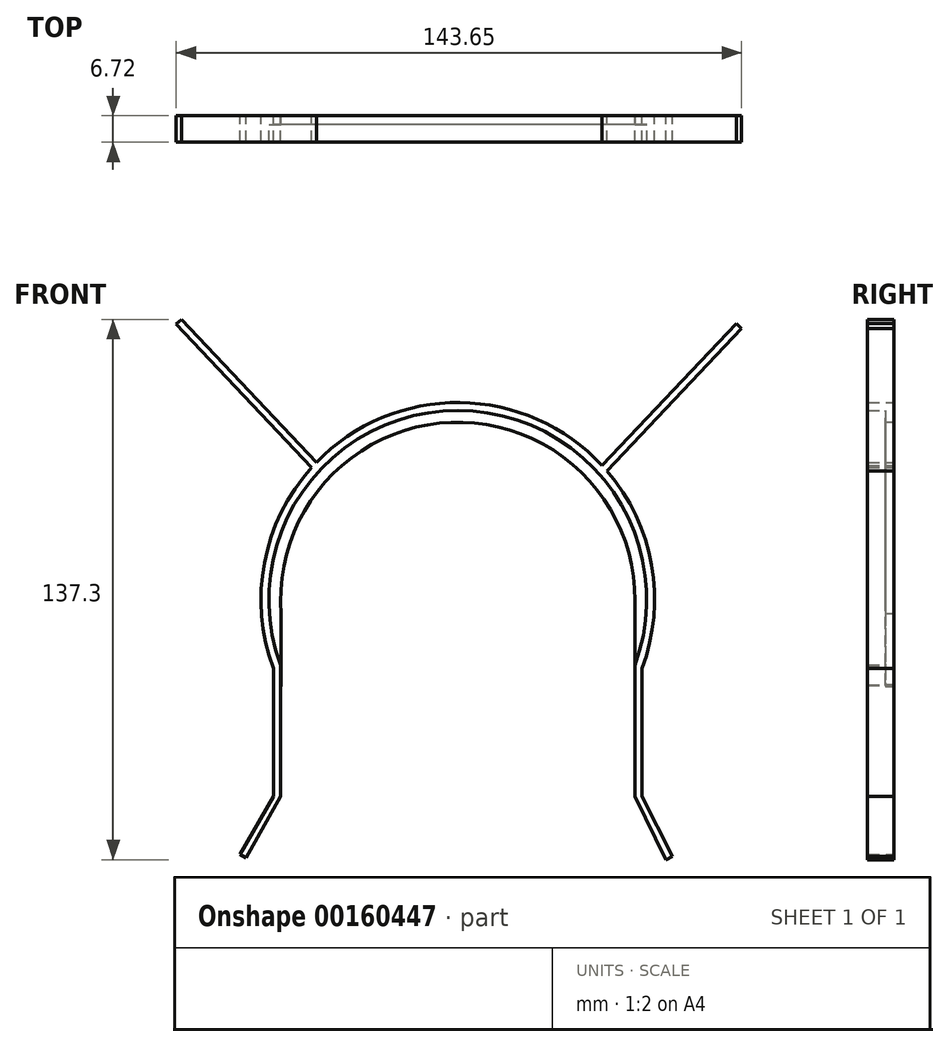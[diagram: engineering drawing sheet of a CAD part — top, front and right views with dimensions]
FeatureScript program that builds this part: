
annotation { "Feature Type Name" : "Feature", "Feature Type Description" : "" }
export const myFeature = defineFeature(function(context is Context, id is Id, definition is map)
    precondition{}
    {
        {
            var Q0;
            Q0=qCreatedBy(makeId("Front.planeOp"),FACE);
            var sketch = newSketch(context, id + "F0", { "sketchPlane" : qUnion([Q0])});
            skLineSegment(sketch, "E0", {"start": v(-45, 0) * mm, "end": v(-45, -50) * mm});
            skLineSegment(sketch, "E1", {"start": v(-45, -50) * mm, "end": v(-46.8, -50) * mm});
            skLineSegment(sketch, "E2", {"start": v(-46.8, -50) * mm, "end": v(-46.8, 0) * mm});
            skLineSegment(sketch, "E3", {"start": v(-46.8, 0) * mm, "end": v(-45, 0) * mm});
            skLineSegment(sketch, "E4", {"start": v(45, 0) * mm, "end": v(45, -50) * mm});
            skLineSegment(sketch, "E5", {"start": v(45, -50) * mm, "end": v(46.8, -50) * mm});
            skLineSegment(sketch, "E6", {"start": v(46.8, -50) * mm, "end": v(46.8, 0) * mm});
            skLineSegment(sketch, "E7", {"start": v(46.8, 0) * mm, "end": v(45, 0) * mm});
            skCircle(sketch, "E8", {"center": v(0, 0) * mm, "radius": 50 * mm});
            skLineSegment(sketch, "E9", {"start": v(-37.12, 33.5) * mm, "end": v(-71.54, 69.91) * mm});
            skLineSegment(sketch, "E10", {"start": v(-71.54, 69.91) * mm, "end": v(-70.23, 71.15) * mm});
            skLineSegment(sketch, "E11", {"start": v(-70.23, 71.15) * mm, "end": v(-35.89, 34.82) * mm});
            skLineSegment(sketch, "E12", {"start": v(36.69, 33.97) * mm, "end": v(70.8, 70.07) * mm});
            skLineSegment(sketch, "E13", {"start": v(70.8, 70.07) * mm, "end": v(72.1, 68.83) * mm});
            skLineSegment(sketch, "E14", {"start": v(72.1, 68.83) * mm, "end": v(37.77, 32.5) * mm});
            skLineSegment(sketch, "E15", {"start": v(-46.8, -50) * mm, "end": v(-55.36, -64.8) * mm});
            skLineSegment(sketch, "E16", {"start": v(-55.36, -64.8) * mm, "end": v(-53.8, -65.7) * mm});
            skLineSegment(sketch, "E17", {"start": v(-53.8, -65.7) * mm, "end": v(-45, -50) * mm});
            skLineSegment(sketch, "E18", {"start": v(45, -50) * mm, "end": v(52.95, -66.15) * mm});
            skLineSegment(sketch, "E19", {"start": v(52.95, -66.15) * mm, "end": v(54.56, -65.36) * mm});
            skLineSegment(sketch, "E20", {"start": v(54.56, -65.36) * mm, "end": v(46.8, -50) * mm});
            skSolve(sketch);
        }
        {
            var Q0;
            Q0=qCreatedBy(makeId("Front.planeOp"),FACE);
            var sketch = newSketch(context, id + "F1", { "sketchPlane" : qUnion([Q0])});
            skSolve(sketch);
        }
        {
            var Q0;
            Q0=qSketchRegion(id+"F1",true);
            var Q1;
            {var subQ0=sQuery(id+"F0.wireOp",EDGE,"E1");Q1=makeQuery(id+"F0.imprint","IMPRINT",FACE,{"disambiguationData":[TD([[makeQuery(id+"F0.imprint","IMPRINT",EDGE,{"derivedFrom":subQ0}),-1.0]])]});}
            var Q2;
            {var subQ0=sQuery(id+"F0.wireOp",EDGE,"E3");Q2=makeQuery(id+"F0.imprint","IMPRINT",FACE,{"disambiguationData":[TD([[makeQuery(id+"F0.imprint","IMPRINT",EDGE,{"derivedFrom":subQ0}),-1.0]])]});}
            var Q3;
            {var subQ0=sQuery(id+"F0.wireOp",EDGE,"E7");Q3=makeQuery(id+"F0.imprint","IMPRINT",FACE,{"disambiguationData":[TD([[makeQuery(id+"F0.imprint","IMPRINT",EDGE,{"derivedFrom":subQ0}),1.0]])]});}
            var Q4;
            {var subQ0=sQuery(id+"F0.wireOp",EDGE,"E5");Q4=makeQuery(id+"F0.imprint","IMPRINT",FACE,{"disambiguationData":[TD([[makeQuery(id+"F0.imprint","IMPRINT",EDGE,{"derivedFrom":subQ0}),1.0]])]});}
            var Q5;
            {var subQ12=sQuery(id+"F0.wireOp",EDGE,"E3");Q5=makeQuery(id+"F0.imprint","IMPRINT",FACE,{"disambiguationData":[TD([[makeQuery(id+"F0.imprint","IMPRINT",EDGE,{"derivedFrom":subQ12}),1.0]])]});}
            var Q6;
            {var subQ0=sQuery(id+"F0.wireOp",EDGE,"E9");Q6=makeQuery(id+"F0.imprint","IMPRINT",FACE,{"disambiguationData":[TD([[makeQuery(id+"F0.imprint","IMPRINT",EDGE,{"derivedFrom":subQ0}),-1.0]])]});}
            var Q7;
            {var subQ0=sQuery(id+"F0.wireOp",EDGE,"E12");Q7=makeQuery(id+"F0.imprint","IMPRINT",FACE,{"disambiguationData":[TD([[makeQuery(id+"F0.imprint","IMPRINT",EDGE,{"derivedFrom":subQ0}),-1.0]])]});}
            var Q8;
            Q8=makeQuery(id+"F0.imprint","IMPRINT",FACE,{"disambiguationData":[TD([[makeQuery(id+"F0.imprint","IMPRINT",EDGE,{"derivedFrom":sQuery(id+"F0.wireOp",EDGE,"E1")}),1.0]])]});
            var Q9;
            Q9=makeQuery(id+"F0.imprint","IMPRINT",FACE,{"disambiguationData":[TD([[makeQuery(id+"F0.imprint","IMPRINT",EDGE,{"derivedFrom":sQuery(id+"F0.wireOp",EDGE,"E5")}),-1.0]])]});
            extrude(context, id + "F2", {"entities" : qUnion([Q0, Q1, Q2, Q3, Q4, Q5, Q6, Q7, Q8, Q9]), "depth" : .5 * mm});
        }
        {
            var Q0;
            Q0=qCreatedBy(makeId("Front.planeOp"),FACE);
            var sketch = newSketch(context, id + "F3", { "sketchPlane" : qUnion([Q0])});
            skCircle(sketch, "E21", {"center": v(0, 0) * mm, "radius": 48 * mm});
            skSolve(sketch);
        }
        {
            var Q0;
            Q0=qSketchRegion(id+"F3",true);
            extrude(context, id + "F4", {"entities" : qUnion([Q0]), "operationType" : NewBodyOperationType.REMOVE, "depth" : 2 * mm});
        }
        {
            var Q0;
            Q0=qCreatedBy(makeId("Front.planeOp"),FACE);
            var sketch = newSketch(context, id + "F5", { "sketchPlane" : qUnion([Q0])});
            skLineSegment(sketch, "E22", {"start": v(44.99, -22.07) * mm, "end": v(44.99, -3.86) * mm});
            skLineSegment(sketch, "E23", {"start": v(44.99, -3.86) * mm, "end": v(-45.01, -3.86) * mm});
            skLineSegment(sketch, "E24", {"start": v(-45.01, -3.86) * mm, "end": v(-45.01, -50.71) * mm});
            skLineSegment(sketch, "E25", {"start": v(-45.01, -50.71) * mm, "end": v(44.99, -50.71) * mm});
            skLineSegment(sketch, "E26", {"start": v(44.99, -50.71) * mm, "end": v(44.99, -22.07) * mm});
            skSolve(sketch);
        }
        {
            var Q0;
            Q0=qCreatedBy(makeId("Front.planeOp"),FACE);
            var sketch = newSketch(context, id + "F6", { "sketchPlane" : qUnion([Q0])});
            skSolve(sketch);
        }
        {
            var Q0;
            Q0=qSketchRegion(id+"F6",true);
            var Q1;
            Q1=makeQuery(id+"F5.imprint","IMPRINT",FACE,{"disambiguationData":[TD([[makeQuery(id+"F5.imprint","IMPRINT",EDGE,{"derivedFrom":sQuery(id+"F5.wireOp",EDGE,"E22")}),1.0]])]});
            extrude(context, id + "F7", {"entities" : qUnion([Q0, Q1]), "operationType" : NewBodyOperationType.REMOVE, "depth" : 2 * mm});
        }
        {
            var Q0;
            Q0=qCreatedBy(makeId("Front.planeOp"),FACE);
            var sketch = newSketch(context, id + "F8", { "sketchPlane" : qUnion([Q0])});
            skCircle(sketch, "E27", {"center": v(0, 0) * mm, "radius": 50 * mm});
            skSolve(sketch);
        }
        {
            var Q0;
            Q0=qSketchRegion(id+"F8",true);
            extrude(context, id + "F9", {"entities" : qUnion([Q0]), "operationType" : NewBodyOperationType.ADD, "oppositeDirection" : true, "depth" : 2.22 * mm});
        }
        {
            var Q0;
            Q0=qCreatedBy(makeId("Front.planeOp"),FACE);
            var sketch = newSketch(context, id + "F10", { "sketchPlane" : qUnion([Q0])});
            skCircle(sketch, "E28", {"center": v(0, 0) * mm, "radius": 45 * mm});
            skSolve(sketch);
        }
        {
            var Q0;
            Q0=qSketchRegion(id+"F10",true);
            extrude(context, id + "F11", {"entities" : qUnion([Q0]), "operationType" : NewBodyOperationType.REMOVE, "oppositeDirection" : true, "depth" : 2.22 * mm});
        }
        {
            var Q0;
            {var subQ0=sQuery(id+"F0.wireOp",EDGE,"E11");var subQ1=sQuery(id+"F0.wireOp",EDGE,"E8");var subQ2=sQuery(id+"F0.wireOp",EDGE,"E12");var subQ3=sQuery(id+"F0.wireOp",EDGE,"E6");var subQ4=sQuery(id+"F0.wireOp",EDGE,"E5");var subQ5=sQuery(id+"F0.wireOp",EDGE,"E4");var subQ6=sQuery(id+"F0.wireOp",EDGE,"E9");var subQ7=sQuery(id+"F0.wireOp",EDGE,"E2");var subQ8=sQuery(id+"F0.wireOp",EDGE,"E0");var subQ9=sQuery(id+"F0.wireOp",EDGE,"E14");Q0=makeQuery(id+"F9.boolean.opBoolean","SPLIT",FACE,{"disambiguationData":[TD([makeQuery(id+"F2.opExtrude","SWEPT_FACE",FACE,{"disambiguationData":[OSD([subQ5])]})])],"derivedFrom":makeQuery(id+"F2.opExtrude","CAP_FACE",FACE,{"disambiguationData":[OSD([subQ8,sQuery(id+"F0.wireOp",EDGE,"E1"),subQ7,subQ5,subQ4,subQ3,subQ1,subQ6,sQuery(id+"F0.wireOp",EDGE,"E10"),subQ0,subQ2,sQuery(id+"F0.wireOp",EDGE,"E13"),subQ9])],"isStart":true})});}
            var Q1;
            {var subQ0=sQuery(id+"F0.wireOp",EDGE,"E9");var subQ1=sQuery(id+"F0.wireOp",EDGE,"E8");var subQ2=sQuery(id+"F0.wireOp",EDGE,"E2");var subQ3=sQuery(id+"F0.wireOp",EDGE,"E11");var subQ4=sQuery(id+"F0.wireOp",EDGE,"E12");var subQ6=sQuery(id+"F0.wireOp",EDGE,"E1");var subQ7=sQuery(id+"F0.wireOp",EDGE,"E0");var subQ8=sQuery(id+"F0.wireOp",EDGE,"E4");var subQ9=sQuery(id+"F0.wireOp",EDGE,"E14");var subQ10=sQuery(id+"F0.wireOp",EDGE,"E6");Q1=makeQuery(id+"F9.boolean.opBoolean","SPLIT",FACE,{"disambiguationData":[TD([makeQuery(id+"F2.opExtrude","SWEPT_FACE",FACE,{"disambiguationData":[OSD([subQ6])]})])],"derivedFrom":makeQuery(id+"F2.opExtrude","CAP_FACE",FACE,{"disambiguationData":[OSD([subQ7,subQ6,subQ2,subQ8,sQuery(id+"F0.wireOp",EDGE,"E5"),subQ10,subQ1,subQ0,sQuery(id+"F0.wireOp",EDGE,"E10"),subQ3,subQ4,sQuery(id+"F0.wireOp",EDGE,"E13"),subQ9])],"isStart":true})});}
            extrude(context, id + "F12", {"entities" : qUnion([Q0, Q1]), "operationType" : NewBodyOperationType.ADD, "depth" : 2.22 * mm});
        }
        {
            var Q0;
            Q0=qCreatedBy(makeId("Front.planeOp"),FACE);
            var sketch = newSketch(context, id + "F13", { "sketchPlane" : qUnion([Q0])});
            skLineSegment(sketch, "E29", {"start": v(45, -21.8) * mm, "end": v(45, 0) * mm});
            skLineSegment(sketch, "E30", {"start": v(45, 0) * mm, "end": v(-44.85, 0) * mm});
            skLineSegment(sketch, "E31", {"start": v(-44.85, 0) * mm, "end": v(-44.85, -53.96) * mm});
            skLineSegment(sketch, "E32", {"start": v(-44.85, -53.96) * mm, "end": v(45, -53.96) * mm});
            skLineSegment(sketch, "E33", {"start": v(45, -53.96) * mm, "end": v(45, -21.8) * mm});
            skSolve(sketch);
        }
        {
            var Q0;
            Q0=makeQuery(id+"F13.imprint","IMPRINT",FACE,{"disambiguationData":[TD([[makeQuery(id+"F13.imprint","IMPRINT",EDGE,{"derivedFrom":sQuery(id+"F13.wireOp",EDGE,"E29")}),1.0]])]});
            extrude(context, id + "F14", {"entities" : qUnion([Q0]), "operationType" : NewBodyOperationType.REMOVE, "oppositeDirection" : true, "depth" : 2.22 * mm});
        }
        {
            var Q0;
            {var subQ0=sQuery(id+"F0.wireOp",EDGE,"E16");var subQ1=sQuery(id+"F0.wireOp",EDGE,"E15");var subQ2=sQuery(id+"F0.wireOp",EDGE,"E14");var subQ3=sQuery(id+"F0.wireOp",EDGE,"E8");var subQ4=sQuery(id+"F0.wireOp",EDGE,"E6");var subQ6=sQuery(id+"F0.wireOp",EDGE,"E2");var subQ7=sQuery(id+"F0.wireOp",EDGE,"E17");var subQ8=sQuery(id+"F0.wireOp",EDGE,"E11");var subQ9=sQuery(id+"F0.wireOp",EDGE,"E12");var subQ10=sQuery(id+"F0.wireOp",EDGE,"E9");var subQ11=sQuery(id+"F0.wireOp",EDGE,"E0");var subQ12=sQuery(id+"F0.wireOp",EDGE,"E4");Q0=makeQuery(id+"F9.boolean.opBoolean","SPLIT",FACE,{"disambiguationData":[TD([makeQuery(id+"F2.opExtrude","SWEPT_FACE",FACE,{"disambiguationData":[OSD([subQ6])]})])],"derivedFrom":makeQuery(id+"F2.opExtrude","CAP_FACE",FACE,{"disambiguationData":[OSD([subQ11,subQ6,subQ12,subQ4,subQ3,subQ10,sQuery(id+"F0.wireOp",EDGE,"E10"),subQ8,subQ9,sQuery(id+"F0.wireOp",EDGE,"E13"),subQ2,subQ1,subQ0,subQ7,sQuery(id+"F0.wireOp",EDGE,"E18"),sQuery(id+"F0.wireOp",EDGE,"E19"),sQuery(id+"F0.wireOp",EDGE,"E20")])],"isStart":true})});}
            var Q1;
            {var subQ0=sQuery(id+"F0.wireOp",EDGE,"E14");var subQ1=sQuery(id+"F0.wireOp",EDGE,"E8");var subQ2=sQuery(id+"F0.wireOp",EDGE,"E6");var subQ3=sQuery(id+"F0.wireOp",EDGE,"E0");var subQ4=sQuery(id+"F0.wireOp",EDGE,"E4");var subQ5=sQuery(id+"F0.wireOp",EDGE,"E9");var subQ6=sQuery(id+"F0.wireOp",EDGE,"E2");var subQ7=sQuery(id+"F0.wireOp",EDGE,"E11");var subQ8=sQuery(id+"F0.wireOp",EDGE,"E12");var subQ9=sQuery(id+"F0.wireOp",EDGE,"E10");Q1=makeQuery(id+"F9.boolean.opBoolean","SPLIT",FACE,{"disambiguationData":[TD([makeQuery(id+"F2.opExtrude","SWEPT_FACE",FACE,{"disambiguationData":[OSD([subQ5])]})])],"derivedFrom":makeQuery(id+"F2.opExtrude","CAP_FACE",FACE,{"disambiguationData":[OSD([subQ3,subQ6,subQ4,subQ2,subQ1,subQ5,subQ9,subQ7,subQ8,sQuery(id+"F0.wireOp",EDGE,"E13"),subQ0,sQuery(id+"F0.wireOp",EDGE,"E15"),sQuery(id+"F0.wireOp",EDGE,"E16"),sQuery(id+"F0.wireOp",EDGE,"E17"),sQuery(id+"F0.wireOp",EDGE,"E18"),sQuery(id+"F0.wireOp",EDGE,"E19"),sQuery(id+"F0.wireOp",EDGE,"E20")])],"isStart":true})});}
            var Q2;
            {var subQ0=sQuery(id+"F0.wireOp",EDGE,"E14");var subQ1=sQuery(id+"F0.wireOp",EDGE,"E8");var subQ2=sQuery(id+"F0.wireOp",EDGE,"E6");var subQ3=sQuery(id+"F0.wireOp",EDGE,"E0");var subQ4=sQuery(id+"F0.wireOp",EDGE,"E4");var subQ5=sQuery(id+"F0.wireOp",EDGE,"E9");var subQ6=sQuery(id+"F0.wireOp",EDGE,"E2");var subQ7=sQuery(id+"F0.wireOp",EDGE,"E13");var subQ8=sQuery(id+"F0.wireOp",EDGE,"E11");var subQ9=sQuery(id+"F0.wireOp",EDGE,"E12");Q2=makeQuery(id+"F9.boolean.opBoolean","SPLIT",FACE,{"disambiguationData":[TD([makeQuery(id+"F2.opExtrude","SWEPT_FACE",FACE,{"disambiguationData":[OSD([subQ9])]})])],"derivedFrom":makeQuery(id+"F2.opExtrude","CAP_FACE",FACE,{"disambiguationData":[OSD([subQ3,subQ6,subQ4,subQ2,subQ1,subQ5,sQuery(id+"F0.wireOp",EDGE,"E10"),subQ8,subQ9,subQ7,subQ0,sQuery(id+"F0.wireOp",EDGE,"E15"),sQuery(id+"F0.wireOp",EDGE,"E16"),sQuery(id+"F0.wireOp",EDGE,"E17"),sQuery(id+"F0.wireOp",EDGE,"E18"),sQuery(id+"F0.wireOp",EDGE,"E19"),sQuery(id+"F0.wireOp",EDGE,"E20")])],"isStart":true})});}
            extrude(context, id + "F15", {"entities" : qUnion([Q0, Q1, Q2]), "operationType" : NewBodyOperationType.ADD, "depth" : 2.22 * mm});
        }
        {
            var Q0;
            Q0=makeQuery(id+"F2.opExtrude","CAP_FACE",FACE,{"disambiguationData":[OSD([sQuery(id+"F0.wireOp",EDGE,"E0"),sQuery(id+"F0.wireOp",EDGE,"E2"),sQuery(id+"F0.wireOp",EDGE,"E4"),sQuery(id+"F0.wireOp",EDGE,"E6"),sQuery(id+"F0.wireOp",EDGE,"E8"),sQuery(id+"F0.wireOp",EDGE,"E9"),sQuery(id+"F0.wireOp",EDGE,"E10"),sQuery(id+"F0.wireOp",EDGE,"E11"),sQuery(id+"F0.wireOp",EDGE,"E12"),sQuery(id+"F0.wireOp",EDGE,"E13"),sQuery(id+"F0.wireOp",EDGE,"E14"),sQuery(id+"F0.wireOp",EDGE,"E15"),sQuery(id+"F0.wireOp",EDGE,"E16"),sQuery(id+"F0.wireOp",EDGE,"E17"),sQuery(id+"F0.wireOp",EDGE,"E18"),sQuery(id+"F0.wireOp",EDGE,"E19"),sQuery(id+"F0.wireOp",EDGE,"E20")])],"isStart":false});
            extrude(context, id + "F16", {"entities" : qUnion([Q0]), "operationType" : NewBodyOperationType.ADD, "depth" : 4 * mm});
        }
    });
